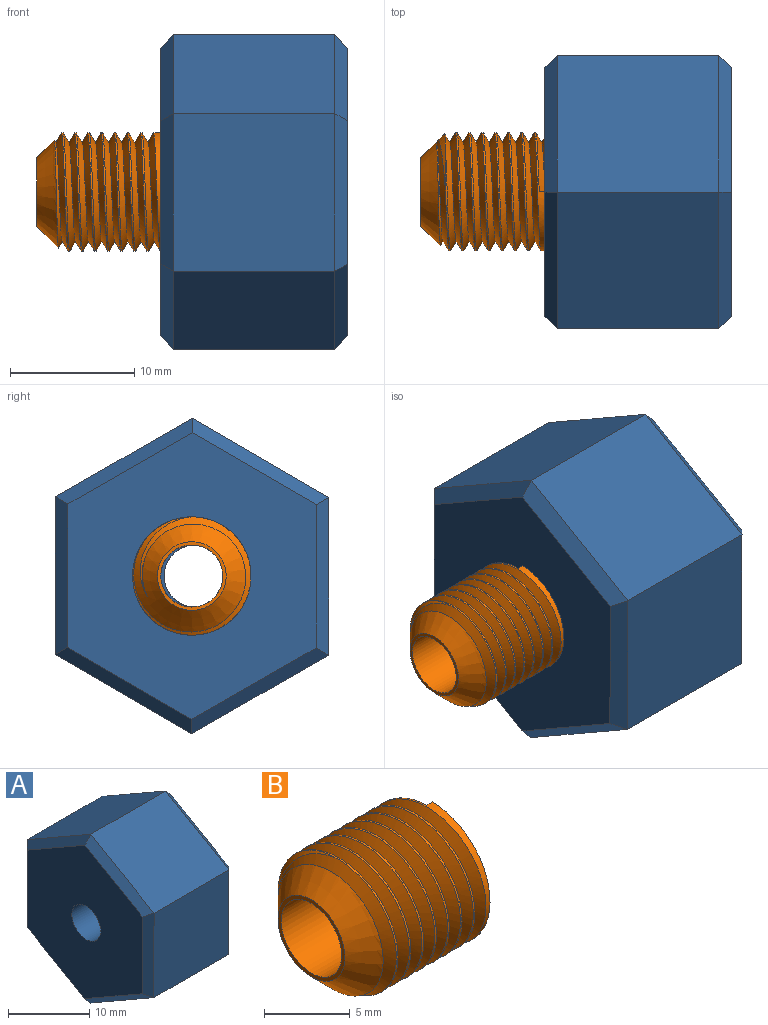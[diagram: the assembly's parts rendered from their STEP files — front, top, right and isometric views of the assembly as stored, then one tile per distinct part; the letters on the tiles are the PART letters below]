
ASSEMBLY  parts=2 mates=1
PART A: 28 faces, bbox 15.3x22.3x25.7 mm
  f0: plane 13x10.98mm, normal (0,-0.5,0.86), area 165.1mm2, adj f1,f5,f13,f17
  f1: plane 13x12.7mm, normal (0,-1,0), area 165.1mm2, adj f0,f2,f11,f15
  f2: plane 13x11.02mm, normal (0,-0.5,-0.87), area 165.1mm2, adj f1,f3,f9,f14
  f3: plane 13x10.98mm, normal (0,0.5,-0.86), area 165.1mm2, adj f2,f4,f8,f16
  f4: plane 13x12.7mm, normal (0,1,0), area 165.1mm2, adj f3,f5,f10,f18
  f5: plane 13x11.02mm, normal (0,0.5,0.87), area 165.1mm2, adj f0,f4,f12,f19
  f6: plane 23.09x20.03mm, normal (-1,0,0), area 326.8mm2, adj f8,f9,f10,f11,f12,f13,f27
  f7: plane 23.09x20.03mm, normal (1,0,0), area 275.2mm2, adj f14,f15,f16,f17,f18,f19,f21
  f8: plane 10.99x6.96mm, normal (-0.71,0.36,-0.61), area 17.1mm2, adj f3,f6,f9,f10
  f9: plane 11.02x6.9mm, normal (-0.71,-0.35,-0.61), area 17.1mm2, adj f2,f6,f8,f11
  f10: plane 12.7x1.03mm, normal (-0.71,0.71,0), area 17.1mm2, adj f4,f6,f8,f12
  f11: plane 12.7x1.03mm, normal (-0.71,-0.71,0), area 17.1mm2, adj f1,f6,f9,f13
  f12: plane 11.02x6.9mm, normal (-0.71,0.35,0.61), area 17.1mm2, adj f5,f6,f10,f13
  f13: plane 10.99x6.96mm, normal (-0.71,-0.36,0.61), area 17.1mm2, adj f0,f6,f11,f12
  f14: plane 11.02x6.9mm, normal (0.71,-0.35,-0.61), area 17.1mm2, adj f2,f7,f15,f16
  f15: plane 12.7x1.03mm, normal (0.71,-0.71,0), area 17.1mm2, adj f1,f7,f14,f17
  f16: plane 10.99x6.96mm, normal (0.71,0.36,-0.61), area 17.1mm2, adj f3,f7,f14,f18
  f17: plane 10.99x6.96mm, normal (0.71,-0.36,0.61), area 17.1mm2, adj f0,f7,f15,f19
  f18: plane 12.7x1.03mm, normal (0.71,0.71,0), area 17.1mm2, adj f4,f7,f16,f19
  f19: plane 11.02x6.9mm, normal (0.71,0.35,0.61), area 17.1mm2, adj f5,f7,f17,f18
  f20: plane 8.57x8.55mm, normal (1,0,0), area 33.8mm2, adj f21,f25,f26,f27
  f21: cone r=4.29mm half-angle=2.7deg, axis (1,0,0), area 93.8mm2, adj f7,f20,f23,f24,f25
  f22: plane 0.68x0.48mm, normal (0,1,0), area 0.2mm2, adj f24,f25,f26
  f23: plane 0.68x0.03mm, normal (0,-0.99,-0.16), area 0mm2, adj f21,f24,f25
  f24: bspline ~10.68x9.81mm, area 211.8mm2, adj f21,f22,f23,f25
  f25: bspline ~10.34x9.81mm, area 18.2mm2, adj f20,f21,f22,f23,f24,f26
  f26: bspline ~8.77x4.48mm, area 2.7mm2, adj f20,f22,f25
  f27: cylinder r=2.5mm len=5mm, axis (-1,0,0), area 78.5mm2, adj f6,f20
PART B: 8 faces, bbox 11.1x11.6x10.1 mm
  f0: cylinder r=4.76mm len=9.53mm, axis (1,0,0), area 52.5mm2, adj f2,f3,f4,f5,f6
  f1: plane 5.53x5.53mm, normal (-1,0,0), area 4.3mm2, adj f3,f7
  f2: plane 10.12x9.79mm, normal (1,0,0), area 46.7mm2, adj f0,f4,f5,f7
  f3: cone r=4.76mm half-angle=45deg, axis (1,0,0), area 52.9mm2, adj f0,f1,f5,f6
  f4: plane 0.8x0.46mm, normal (0,1,0), area 0.2mm2, adj f0,f2,f6
  f5: bspline ~11x9.53mm, area 201.3mm2, adj f0,f2,f3,f6
  f6: bspline ~11x9.53mm, area 197.4mm2, adj f0,f3,f4,f5
  f7: cylinder r=2.5mm len=10mm, axis (1,0,0), area 157.1mm2, adj f1,f2
PLACE A t=(35.19,2.26,3.07)mm
PLACE B t=(20.19,2.27,3.07)mm
MATE fastened B.f0 <-> A.f6  axis (1,0,0) through (20.19,2.27,3.07)mm
